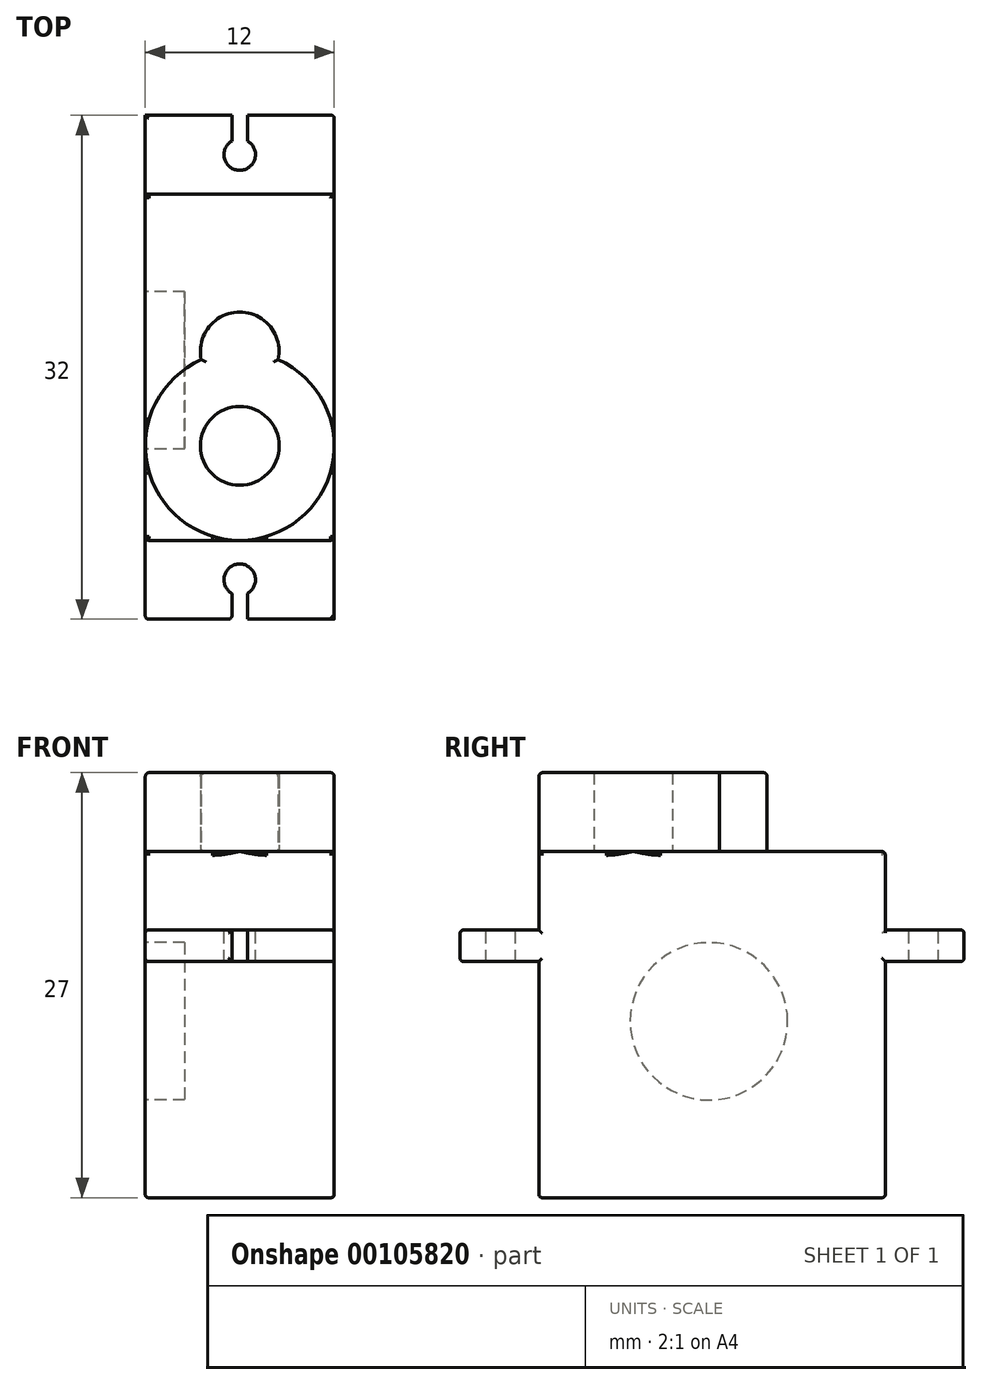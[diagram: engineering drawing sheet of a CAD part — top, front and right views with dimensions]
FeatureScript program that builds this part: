
annotation { "Feature Type Name" : "Feature", "Feature Type Description" : "" }
export const myFeature = defineFeature(function(context is Context, id is Id, definition is map)
    precondition{}
    {
        {
            var Q0;
            Q0=qCreatedBy(makeId("Top.planeOp"),FACE);
            var sketch = newSketch(context, id + "F0", { "sketchPlane" : qUnion([Q0])});
            skLineSegment(sketch, "E0.bottom", {"start": v(-8.25, -0.4) * mm, "end": v(3.75, -0.4) * mm});
            skLineSegment(sketch, "E0.top", {"start": v(-8.25, -22.4) * mm, "end": v(3.75, -22.4) * mm});
            skLineSegment(sketch, "E0.left", {"start": v(-8.25, -0.4) * mm, "end": v(-8.25, -22.4) * mm});
            skLineSegment(sketch, "E0.right", {"start": v(3.75, -0.4) * mm, "end": v(3.75, -22.4) * mm});
            skSolve(sketch);
        }
        {
            var Q0;
            Q0=makeQuery(id+"F0.imprint","IMPRINT",FACE,{"disambiguationData":[TD([[makeQuery(id+"F0.imprint","IMPRINT",EDGE,{"derivedFrom":sQuery(id+"F0.wireOp",EDGE,"E0.bottom")}),-1.0]])]});
            extrude(context, id + "F1", {"entities" : qUnion([Q0]), "depth" : 22 * mm});
        }
        {
            var Q0;
            Q0=makeQuery(id+"F1.opExtrude","CAP_FACE",FACE,{"disambiguationData":[OSD([sQuery(id+"F0.wireOp",EDGE,"E0.bottom"),sQuery(id+"F0.wireOp",EDGE,"E0.top"),sQuery(id+"F0.wireOp",EDGE,"E0.left"),sQuery(id+"F0.wireOp",EDGE,"E0.right")])],"isStart":false});
            var sketch = newSketch(context, id + "F2", { "sketchPlane" : qUnion([Q0])});
            skCircle(sketch, "E1", {"center": v(-2.25, -16.4) * mm, "radius": 6 * mm});
            skCircle(sketch, "E2", {"center": v(-2.25, -16.4) * mm, "radius": 2.5 * mm});
            skCircle(sketch, "E3", {"center": v(-2.25, -10.4) * mm, "radius": 2.5 * mm});
            skSolve(sketch);
        }
        {
            var Q0;
            {var subQ0=sQuery(id+"F2.wireOp",EDGE,"E3");var subQ1=sQuery(id+"F2.wireOp",EDGE,"E1");var subQ3=makeQuery(id+"F2.imprint","INTERSECT",VERTEX,{"disambiguationData":[OD(0.0)],"derivedFrom":[subQ1,subQ0]});Q0=makeQuery(id+"F2.imprint","IMPRINT",FACE,{"disambiguationData":[TD([[makeQuery(id+"F2.imprint","IMPRINT",EDGE,{"disambiguationData":[TD([[subQ3,-1.0]])],"derivedFrom":subQ1}),-1.0]])]});}
            var Q1;
            {var subQ0=sQuery(id+"F2.wireOp",EDGE,"E3");var subQ1=sQuery(id+"F2.wireOp",EDGE,"E1");var subQ3=makeQuery(id+"F2.imprint","INTERSECT",VERTEX,{"disambiguationData":[OD(0.0)],"derivedFrom":[subQ1,subQ0]});Q1=makeQuery(id+"F2.imprint","IMPRINT",FACE,{"disambiguationData":[TD([[makeQuery(id+"F2.imprint","IMPRINT",EDGE,{"disambiguationData":[TD([[subQ3,-1.0]])],"derivedFrom":subQ1}),1.0]])]});}
            var Q2;
            Q2=makeQuery(id+"F2.imprint","IMPRINT",FACE,{"disambiguationData":[TD([[makeQuery(id+"F2.imprint","IMPRINT",EDGE,{"derivedFrom":sQuery(id+"F2.wireOp",EDGE,"E2")}),-1.0]])]});
            extrude(context, id + "F3", {"entities" : qUnion([Q0, Q1, Q2]), "operationType" : NewBodyOperationType.ADD, "depth" : 5 * mm});
        }
        {
            var Q0;
            Q0=makeQuery(id+"F3.opExtrude","CAP_EDGE",EDGE,{"disambiguationData":[OSD([sQuery(id+"F2.wireOp",EDGE,"E1")])],"isStart":false});
            var Q1;
            Q1=makeQuery(id+"F3.opExtrude","CAP_EDGE",EDGE,{"disambiguationData":[OSD([sQuery(id+"F2.wireOp",EDGE,"E3")])],"isStart":false});
            var Q2;
            {var subQ0=sQuery(id+"F0.wireOp",EDGE,"E0.right");var subQ1=sQuery(id+"F0.wireOp",EDGE,"E0.bottom");Q2=makeQuery(id+"F3.boolean.opBoolean","SPLIT",EDGE,{"disambiguationData":[TD([makeQuery(id+"F1.opExtrude","SWEPT_FACE",FACE,{"disambiguationData":[OSD([subQ1])]})])],"derivedFrom":makeQuery(id+"F1.opExtrude","CAP_EDGE",EDGE,{"disambiguationData":[OSD([subQ0])],"isStart":false})});}
            var Q3;
            Q3=makeQuery(id+"F1.opExtrude","CAP_EDGE",EDGE,{"disambiguationData":[OSD([sQuery(id+"F0.wireOp",EDGE,"E0.bottom")])],"isStart":false});
            var Q4;
            {var subQ0=sQuery(id+"F0.wireOp",EDGE,"E0.left");var subQ1=sQuery(id+"F0.wireOp",EDGE,"E0.bottom");Q4=makeQuery(id+"F3.boolean.opBoolean","SPLIT",EDGE,{"disambiguationData":[TD([makeQuery(id+"F1.opExtrude","SWEPT_FACE",FACE,{"disambiguationData":[OSD([subQ1])]})])],"derivedFrom":makeQuery(id+"F1.opExtrude","CAP_EDGE",EDGE,{"disambiguationData":[OSD([subQ0])],"isStart":false})});}
            var Q5;
            {var subQ0=sQuery(id+"F0.wireOp",EDGE,"E0.right");var subQ1=sQuery(id+"F0.wireOp",EDGE,"E0.top");Q5=makeQuery(id+"F3.boolean.opBoolean","SPLIT",EDGE,{"disambiguationData":[TD([makeQuery(id+"F1.opExtrude","SWEPT_FACE",FACE,{"disambiguationData":[OSD([subQ1])]})])],"derivedFrom":makeQuery(id+"F1.opExtrude","CAP_EDGE",EDGE,{"disambiguationData":[OSD([subQ0])],"isStart":false})});}
            var Q6;
            {var subQ0=sQuery(id+"F0.wireOp",EDGE,"E0.top");var subQ1=sQuery(id+"F0.wireOp",EDGE,"E0.right");Q6=makeQuery(id+"F3.boolean.opBoolean","SPLIT",EDGE,{"disambiguationData":[TD([makeQuery(id+"F1.opExtrude","SWEPT_FACE",FACE,{"disambiguationData":[OSD([subQ1])]})])],"derivedFrom":makeQuery(id+"F1.opExtrude","CAP_EDGE",EDGE,{"disambiguationData":[OSD([subQ0])],"isStart":false})});}
            var Q7;
            {var subQ0=sQuery(id+"F0.wireOp",EDGE,"E0.top");var subQ1=sQuery(id+"F0.wireOp",EDGE,"E0.left");Q7=makeQuery(id+"F3.boolean.opBoolean","SPLIT",EDGE,{"disambiguationData":[TD([makeQuery(id+"F1.opExtrude","SWEPT_FACE",FACE,{"disambiguationData":[OSD([subQ1])]})])],"derivedFrom":makeQuery(id+"F1.opExtrude","CAP_EDGE",EDGE,{"disambiguationData":[OSD([subQ0])],"isStart":false})});}
            var Q8;
            {var subQ0=sQuery(id+"F0.wireOp",EDGE,"E0.left");var subQ1=sQuery(id+"F0.wireOp",EDGE,"E0.top");Q8=makeQuery(id+"F3.boolean.opBoolean","SPLIT",EDGE,{"disambiguationData":[TD([makeQuery(id+"F1.opExtrude","SWEPT_FACE",FACE,{"disambiguationData":[OSD([subQ1])]})])],"derivedFrom":makeQuery(id+"F1.opExtrude","CAP_EDGE",EDGE,{"disambiguationData":[OSD([subQ0])],"isStart":false})});}
            fillet(context, id + "F4", {"entities" : qUnion([Q0, Q1, Q2, Q3, Q4, Q5, Q6, Q7, Q8]), "radius" : .25 * mm, "tangentPropagation" : true, "allowEdgeOverflow" : false});
        }
        {
            var Q0;
            Q0=makeQuery(id+"F1.opExtrude","SWEPT_FACE",FACE,{"disambiguationData":[OSD([sQuery(id+"F0.wireOp",EDGE,"E0.bottom")])]});
            var sketch = newSketch(context, id + "F5", { "sketchPlane" : qUnion([Q0])});
            skLineSegment(sketch, "E4.bottom", {"start": v(-3.75, 17) * mm, "end": v(8.25, 17) * mm});
            skLineSegment(sketch, "E4.top", {"start": v(-3.75, 15) * mm, "end": v(8.25, 15) * mm});
            skLineSegment(sketch, "E4.left", {"start": v(-3.75, 17) * mm, "end": v(-3.75, 15) * mm});
            skLineSegment(sketch, "E4.right", {"start": v(8.25, 17) * mm, "end": v(8.25, 15) * mm});
            skSolve(sketch);
        }
        {
            var Q0;
            Q0=makeQuery(id+"F1.opExtrude","SWEPT_FACE",FACE,{"disambiguationData":[OSD([sQuery(id+"F0.wireOp",EDGE,"E0.top")])]});
            var sketch = newSketch(context, id + "F6", { "sketchPlane" : qUnion([Q0])});
            skLineSegment(sketch, "E5.bottom", {"start": v(-8.25, 17) * mm, "end": v(3.75, 17) * mm});
            skLineSegment(sketch, "E5.top", {"start": v(-8.25, 15) * mm, "end": v(3.75, 15) * mm});
            skLineSegment(sketch, "E5.left", {"start": v(-8.25, 17) * mm, "end": v(-8.25, 15) * mm});
            skLineSegment(sketch, "E5.right", {"start": v(3.75, 17) * mm, "end": v(3.75, 15) * mm});
            skSolve(sketch);
        }
        {
            var Q0;
            Q0=makeQuery(id+"F6.imprint","IMPRINT",FACE,{"disambiguationData":[TD([[makeQuery(id+"F6.imprint","IMPRINT",EDGE,{"derivedFrom":sQuery(id+"F6.wireOp",EDGE,"E5.bottom")}),-1.0]])]});
            extrude(context, id + "F7", {"entities" : qUnion([Q0]), "operationType" : NewBodyOperationType.ADD, "depth" : 5 * mm});
        }
        {
            var Q0;
            Q0=makeQuery(id+"F5.imprint","IMPRINT",FACE,{"disambiguationData":[TD([[makeQuery(id+"F5.imprint","IMPRINT",EDGE,{"derivedFrom":sQuery(id+"F5.wireOp",EDGE,"E4.bottom")}),-1.0]])]});
            extrude(context, id + "F8", {"entities" : qUnion([Q0]), "operationType" : NewBodyOperationType.ADD, "depth" : 5 * mm});
        }
        {
            var Q0;
            Q0=makeQuery(id+"F7.opExtrude","SWEPT_FACE",FACE,{"disambiguationData":[OSD([sQuery(id+"F6.wireOp",EDGE,"E5.bottom")])]});
            var sketch = newSketch(context, id + "F9", { "sketchPlane" : qUnion([Q0])});
            skCircle(sketch, "E6", {"center": v(-2.25, -24.9) * mm, "radius": 1 * mm});
            skLineSegment(sketch, "E7.bottom", {"start": v(-2.75, -25.77) * mm, "end": v(-1.75, -25.77) * mm});
            skLineSegment(sketch, "E7.top", {"start": v(-2.75, -27.4) * mm, "end": v(-1.75, -27.4) * mm});
            skLineSegment(sketch, "E7.left", {"start": v(-2.75, -25.77) * mm, "end": v(-2.75, -27.4) * mm});
            skLineSegment(sketch, "E7.right", {"start": v(-1.75, -25.77) * mm, "end": v(-1.75, -27.4) * mm});
            skSolve(sketch);
        }
        {
            var Q0;
            {var subQ0=sQuery(id+"F9.wireOp",EDGE,"E7.bottom");Q0=makeQuery(id+"F9.imprint","IMPRINT",FACE,{"disambiguationData":[TD([[makeQuery(id+"F9.imprint","IMPRINT",EDGE,{"derivedFrom":subQ0}),1.0]])]});}
            var Q1;
            Q1=makeQuery(id+"F9.imprint","IMPRINT",FACE,{"disambiguationData":[TD([[makeQuery(id+"F9.imprint","IMPRINT",EDGE,{"derivedFrom":sQuery(id+"F9.wireOp",EDGE,"E7.top")}),1.0]])]});
            var Q2;
            {var subQ0=sQuery(id+"F9.wireOp",EDGE,"E7.bottom");Q2=makeQuery(id+"F9.imprint","IMPRINT",FACE,{"disambiguationData":[TD([[makeQuery(id+"F9.imprint","IMPRINT",EDGE,{"derivedFrom":subQ0}),-1.0]])]});}
            extrude(context, id + "F10", {"entities" : qUnion([Q0, Q1, Q2]), "operationType" : NewBodyOperationType.REMOVE, "oppositeDirection" : true, "depth" : 2 * mm});
        }
        {
            var Q0;
            Q0=makeQuery(id+"F8.opExtrude","SWEPT_FACE",FACE,{"disambiguationData":[OSD([sQuery(id+"F5.wireOp",EDGE,"E4.bottom")])]});
            var sketch = newSketch(context, id + "F11", { "sketchPlane" : qUnion([Q0])});
            skCircle(sketch, "E8", {"center": v(-2.25, 2.1) * mm, "radius": 1 * mm});
            skLineSegment(sketch, "E9.bottom", {"start": v(-2.75, 4.6) * mm, "end": v(-1.75, 4.6) * mm});
            skLineSegment(sketch, "E9.top", {"start": v(-2.75, 2.6) * mm, "end": v(-1.75, 2.6) * mm});
            skLineSegment(sketch, "E9.left", {"start": v(-2.75, 4.6) * mm, "end": v(-2.75, 2.6) * mm});
            skLineSegment(sketch, "E9.right", {"start": v(-1.75, 4.6) * mm, "end": v(-1.75, 2.6) * mm});
            skSolve(sketch);
        }
        {
            var Q0;
            Q0=qSketchRegion(id+"F11",true);
            extrude(context, id + "F12", {"entities" : qUnion([Q0]), "operationType" : NewBodyOperationType.REMOVE, "oppositeDirection" : true, "depth" : 2 * mm});
        }
        {
            var Q0;
            Q0=makeQuery(id+"F8.opExtrude","SWEPT_EDGE",EDGE,{"disambiguationData":[OSD([sQuery(id+"F0.wireOp",EDGE,"E0.bottom"),sQuery(id+"F0.wireOp",EDGE,"E0.left"),sQuery(id+"F5.wireOp",EDGE,"E4.bottom"),sQuery(id+"F5.wireOp",EDGE,"E4.right")])]});
            var Q1;
            {var subQ0=sQuery(id+"F5.wireOp",EDGE,"E4.bottom");Q1=makeQuery(id+"F12.boolean.opBoolean","SPLIT",EDGE,{"disambiguationData":[TD([makeQuery(id+"F1.opExtrude","SWEPT_FACE",FACE,{"disambiguationData":[OSD([sQuery(id+"F0.wireOp",EDGE,"E0.left")])]})])],"derivedFrom":makeQuery(id+"F8.opExtrude","CAP_EDGE",EDGE,{"disambiguationData":[OSD([subQ0])],"isStart":false})});}
            var Q2;
            Q2=makeQuery(id+"F12.boolean.opBoolean","COPY",EDGE,{"derivedFrom":makeQuery(id+"F12.opExtrude","CAP_EDGE",EDGE,{"disambiguationData":[OSD([sQuery(id+"F11.wireOp",EDGE,"E9.left")])],"isStart":true})});
            var Q3;
            Q3=makeQuery(id+"F12.boolean.opBoolean","COPY",EDGE,{"derivedFrom":makeQuery(id+"F12.opExtrude","CAP_EDGE",EDGE,{"disambiguationData":[OSD([sQuery(id+"F11.wireOp",EDGE,"E8")])],"isStart":true})});
            var Q4;
            Q4=makeQuery(id+"F12.boolean.opBoolean","COPY",EDGE,{"derivedFrom":makeQuery(id+"F12.opExtrude","CAP_EDGE",EDGE,{"disambiguationData":[OSD([sQuery(id+"F11.wireOp",EDGE,"E9.right")])],"isStart":true})});
            var Q5;
            {var subQ0=sQuery(id+"F5.wireOp",EDGE,"E4.bottom");Q5=makeQuery(id+"F12.boolean.opBoolean","SPLIT",EDGE,{"disambiguationData":[TD([makeQuery(id+"F1.opExtrude","SWEPT_FACE",FACE,{"disambiguationData":[OSD([sQuery(id+"F0.wireOp",EDGE,"E0.right")])]})])],"derivedFrom":makeQuery(id+"F8.opExtrude","CAP_EDGE",EDGE,{"disambiguationData":[OSD([subQ0])],"isStart":false})});}
            var Q6;
            Q6=makeQuery(id+"F8.opExtrude","SWEPT_EDGE",EDGE,{"disambiguationData":[OSD([sQuery(id+"F0.wireOp",EDGE,"E0.bottom"),sQuery(id+"F0.wireOp",EDGE,"E0.right"),sQuery(id+"F5.wireOp",EDGE,"E4.bottom"),sQuery(id+"F5.wireOp",EDGE,"E4.left")])]});
            var Q7;
            Q7=makeQuery(id+"F7.opExtrude","SWEPT_EDGE",EDGE,{"disambiguationData":[OSD([sQuery(id+"F0.wireOp",EDGE,"E0.top"),sQuery(id+"F0.wireOp",EDGE,"E0.right"),sQuery(id+"F6.wireOp",EDGE,"E5.bottom"),sQuery(id+"F6.wireOp",EDGE,"E5.right")])]});
            var Q8;
            {var subQ0=sQuery(id+"F6.wireOp",EDGE,"E5.bottom");Q8=makeQuery(id+"F10.boolean.opBoolean","SPLIT",EDGE,{"disambiguationData":[TD([makeQuery(id+"F1.opExtrude","SWEPT_FACE",FACE,{"disambiguationData":[OSD([sQuery(id+"F0.wireOp",EDGE,"E0.right")])]})])],"derivedFrom":makeQuery(id+"F7.opExtrude","CAP_EDGE",EDGE,{"disambiguationData":[OSD([subQ0])],"isStart":false})});}
            var Q9;
            {var subQ0=sQuery(id+"F6.wireOp",EDGE,"E5.top");Q9=makeQuery(id+"F10.boolean.opBoolean","SPLIT",EDGE,{"disambiguationData":[TD([makeQuery(id+"F1.opExtrude","SWEPT_FACE",FACE,{"disambiguationData":[OSD([sQuery(id+"F0.wireOp",EDGE,"E0.right")])]})])],"derivedFrom":makeQuery(id+"F7.opExtrude","CAP_EDGE",EDGE,{"disambiguationData":[OSD([subQ0])],"isStart":false})});}
            var Q10;
            Q10=makeQuery(id+"F7.opExtrude","SWEPT_EDGE",EDGE,{"disambiguationData":[OSD([sQuery(id+"F0.wireOp",EDGE,"E0.top"),sQuery(id+"F0.wireOp",EDGE,"E0.right"),sQuery(id+"F6.wireOp",EDGE,"E5.top"),sQuery(id+"F6.wireOp",EDGE,"E5.right")])]});
            var Q11;
            Q11=makeQuery(id+"F10.boolean.opBoolean","COPY",EDGE,{"derivedFrom":makeQuery(id+"F10.opExtrude","SWEPT_EDGE",EDGE,{"disambiguationData":[OSD([sQuery(id+"F6.wireOp",EDGE,"E5.bottom"),sQuery(id+"F9.wireOp",EDGE,"E7.top"),sQuery(id+"F9.wireOp",EDGE,"E7.right")])]})});
            var Q12;
            Q12=makeQuery(id+"F10.boolean.opBoolean","COPY",EDGE,{"derivedFrom":makeQuery(id+"F10.opExtrude","SWEPT_EDGE",EDGE,{"disambiguationData":[OSD([sQuery(id+"F6.wireOp",EDGE,"E5.bottom"),sQuery(id+"F9.wireOp",EDGE,"E7.top"),sQuery(id+"F9.wireOp",EDGE,"E7.left")])]})});
            var Q13;
            Q13=makeQuery(id+"F10.boolean.opBoolean","COPY",EDGE,{"derivedFrom":makeQuery(id+"F10.opExtrude","CAP_EDGE",EDGE,{"disambiguationData":[OSD([sQuery(id+"F9.wireOp",EDGE,"E7.left")])],"isStart":true})});
            var Q14;
            Q14=makeQuery(id+"F10.boolean.opBoolean","COPY",EDGE,{"derivedFrom":makeQuery(id+"F10.opExtrude","CAP_EDGE",EDGE,{"disambiguationData":[OSD([sQuery(id+"F9.wireOp",EDGE,"E6")])],"isStart":true})});
            var Q15;
            Q15=makeQuery(id+"F10.boolean.opBoolean","COPY",EDGE,{"derivedFrom":makeQuery(id+"F10.opExtrude","CAP_EDGE",EDGE,{"disambiguationData":[OSD([sQuery(id+"F9.wireOp",EDGE,"E7.left")])],"isStart":false})});
            var Q16;
            Q16=makeQuery(id+"F10.boolean.opBoolean","COPY",EDGE,{"derivedFrom":makeQuery(id+"F10.opExtrude","CAP_EDGE",EDGE,{"disambiguationData":[OSD([sQuery(id+"F9.wireOp",EDGE,"E6")])],"isStart":false})});
            var Q17;
            {var subQ0=sQuery(id+"F6.wireOp",EDGE,"E5.top");Q17=makeQuery(id+"F10.boolean.opBoolean","SPLIT",EDGE,{"disambiguationData":[TD([makeQuery(id+"F1.opExtrude","SWEPT_FACE",FACE,{"disambiguationData":[OSD([sQuery(id+"F0.wireOp",EDGE,"E0.left")])]})])],"derivedFrom":makeQuery(id+"F7.opExtrude","CAP_EDGE",EDGE,{"disambiguationData":[OSD([subQ0])],"isStart":false})});}
            var Q18;
            {var subQ0=sQuery(id+"F6.wireOp",EDGE,"E5.bottom");Q18=makeQuery(id+"F10.boolean.opBoolean","SPLIT",EDGE,{"disambiguationData":[TD([makeQuery(id+"F1.opExtrude","SWEPT_FACE",FACE,{"disambiguationData":[OSD([sQuery(id+"F0.wireOp",EDGE,"E0.left")])]})])],"derivedFrom":makeQuery(id+"F7.opExtrude","CAP_EDGE",EDGE,{"disambiguationData":[OSD([subQ0])],"isStart":false})});}
            var Q19;
            Q19=makeQuery(id+"F7.opExtrude","CAP_EDGE",EDGE,{"disambiguationData":[OSD([sQuery(id+"F6.wireOp",EDGE,"E5.left")])],"isStart":false});
            var Q20;
            {var subQ0=sQuery(id+"F0.wireOp",EDGE,"E0.top");var subQ1=sQuery(id+"F0.wireOp",EDGE,"E0.right");Q20=makeQuery(id+"F7.boolean.opBoolean","SPLIT",EDGE,{"disambiguationData":[TD([makeQuery(id+"F7.opExtrude","SWEPT_FACE",FACE,{"disambiguationData":[OSD([sQuery(id+"F6.wireOp",EDGE,"E5.top")])]})])],"derivedFrom":makeQuery(id+"F1.opExtrude","SWEPT_EDGE",EDGE,{"disambiguationData":[OSD([subQ0,subQ1])]})});}
            var Q21;
            {var subQ0=sQuery(id+"F0.wireOp",EDGE,"E0.top");var subQ1=sQuery(id+"F0.wireOp",EDGE,"E0.right");Q21=makeQuery(id+"F7.boolean.opBoolean","SPLIT",EDGE,{"disambiguationData":[TD([makeQuery(id+"F7.opExtrude","SWEPT_FACE",FACE,{"disambiguationData":[OSD([sQuery(id+"F6.wireOp",EDGE,"E5.bottom")])]})])],"derivedFrom":makeQuery(id+"F1.opExtrude","SWEPT_EDGE",EDGE,{"disambiguationData":[OSD([subQ0,subQ1])]})});}
            var Q22;
            {var subQ0=sQuery(id+"F0.wireOp",EDGE,"E0.top");var subQ1=sQuery(id+"F0.wireOp",EDGE,"E0.left");Q22=makeQuery(id+"F7.boolean.opBoolean","SPLIT",EDGE,{"disambiguationData":[TD([makeQuery(id+"F7.opExtrude","SWEPT_FACE",FACE,{"disambiguationData":[OSD([sQuery(id+"F6.wireOp",EDGE,"E5.bottom")])]})])],"derivedFrom":makeQuery(id+"F1.opExtrude","SWEPT_EDGE",EDGE,{"disambiguationData":[OSD([subQ0,subQ1])]})});}
            var Q23;
            Q23=makeQuery(id+"F10.boolean.opBoolean","COPY",EDGE,{"derivedFrom":makeQuery(id+"F10.opExtrude","CAP_EDGE",EDGE,{"disambiguationData":[OSD([sQuery(id+"F9.wireOp",EDGE,"E7.right")])],"isStart":false})});
            var Q24;
            Q24=makeQuery(id+"F7.opExtrude","SWEPT_EDGE",EDGE,{"disambiguationData":[OSD([sQuery(id+"F0.wireOp",EDGE,"E0.top"),sQuery(id+"F0.wireOp",EDGE,"E0.left"),sQuery(id+"F6.wireOp",EDGE,"E5.top"),sQuery(id+"F6.wireOp",EDGE,"E5.left")])]});
            var Q25;
            Q25=makeQuery(id+"F7.opExtrude","SWEPT_EDGE",EDGE,{"disambiguationData":[OSD([sQuery(id+"F0.wireOp",EDGE,"E0.top"),sQuery(id+"F0.wireOp",EDGE,"E0.left"),sQuery(id+"F6.wireOp",EDGE,"E5.bottom"),sQuery(id+"F6.wireOp",EDGE,"E5.left")])]});
            var Q26;
            {var subQ0=sQuery(id+"F0.wireOp",EDGE,"E0.top");var subQ1=sQuery(id+"F0.wireOp",EDGE,"E0.left");Q26=makeQuery(id+"F7.boolean.opBoolean","SPLIT",EDGE,{"disambiguationData":[TD([makeQuery(id+"F7.opExtrude","SWEPT_FACE",FACE,{"disambiguationData":[OSD([sQuery(id+"F6.wireOp",EDGE,"E5.top")])]})])],"derivedFrom":makeQuery(id+"F1.opExtrude","SWEPT_EDGE",EDGE,{"disambiguationData":[OSD([subQ0,subQ1])]})});}
            var Q27;
            Q27=makeQuery(id+"F1.opExtrude","CAP_EDGE",EDGE,{"disambiguationData":[OSD([sQuery(id+"F0.wireOp",EDGE,"E0.left")])],"isStart":true});
            var Q28;
            Q28=makeQuery(id+"F1.opExtrude","CAP_EDGE",EDGE,{"disambiguationData":[OSD([sQuery(id+"F0.wireOp",EDGE,"E0.top")])],"isStart":true});
            var Q29;
            {var subQ0=sQuery(id+"F0.wireOp",EDGE,"E0.bottom");var subQ1=sQuery(id+"F0.wireOp",EDGE,"E0.left");Q29=makeQuery(id+"F8.boolean.opBoolean","SPLIT",EDGE,{"disambiguationData":[TD([makeQuery(id+"F8.opExtrude","SWEPT_FACE",FACE,{"disambiguationData":[OSD([sQuery(id+"F5.wireOp",EDGE,"E4.top")])]})])],"derivedFrom":makeQuery(id+"F1.opExtrude","SWEPT_EDGE",EDGE,{"disambiguationData":[OSD([subQ0,subQ1])]})});}
            var Q30;
            Q30=makeQuery(id+"F8.opExtrude","SWEPT_EDGE",EDGE,{"disambiguationData":[OSD([sQuery(id+"F0.wireOp",EDGE,"E0.bottom"),sQuery(id+"F0.wireOp",EDGE,"E0.left"),sQuery(id+"F5.wireOp",EDGE,"E4.top"),sQuery(id+"F5.wireOp",EDGE,"E4.right")])]});
            var Q31;
            {var subQ0=sQuery(id+"F5.wireOp",EDGE,"E4.top");Q31=makeQuery(id+"F12.boolean.opBoolean","SPLIT",EDGE,{"disambiguationData":[TD([makeQuery(id+"F1.opExtrude","SWEPT_FACE",FACE,{"disambiguationData":[OSD([sQuery(id+"F0.wireOp",EDGE,"E0.left")])]})])],"derivedFrom":makeQuery(id+"F8.opExtrude","CAP_EDGE",EDGE,{"disambiguationData":[OSD([subQ0])],"isStart":false})});}
            var Q32;
            Q32=makeQuery(id+"F12.boolean.opBoolean","COPY",EDGE,{"derivedFrom":makeQuery(id+"F12.opExtrude","CAP_EDGE",EDGE,{"disambiguationData":[OSD([sQuery(id+"F11.wireOp",EDGE,"E8")])],"isStart":false})});
            var Q33;
            Q33=makeQuery(id+"F12.boolean.opBoolean","COPY",EDGE,{"derivedFrom":makeQuery(id+"F12.opExtrude","CAP_EDGE",EDGE,{"disambiguationData":[OSD([sQuery(id+"F11.wireOp",EDGE,"E9.left")])],"isStart":false})});
            var Q34;
            Q34=makeQuery(id+"F12.boolean.opBoolean","COPY",EDGE,{"derivedFrom":makeQuery(id+"F12.opExtrude","CAP_EDGE",EDGE,{"disambiguationData":[OSD([sQuery(id+"F11.wireOp",EDGE,"E9.right")])],"isStart":false})});
            var Q35;
            {var subQ0=sQuery(id+"F0.wireOp",EDGE,"E0.bottom");var subQ1=sQuery(id+"F0.wireOp",EDGE,"E0.left");Q35=makeQuery(id+"F8.boolean.opBoolean","SPLIT",EDGE,{"disambiguationData":[TD([makeQuery(id+"F4.opFillet","BLEND_FACE",FACE,{"disambiguationData":[OSD([subQ0])]})])],"derivedFrom":makeQuery(id+"F1.opExtrude","SWEPT_EDGE",EDGE,{"disambiguationData":[OSD([subQ0,subQ1])]})});}
            var Q36;
            {var subQ0=sQuery(id+"F0.wireOp",EDGE,"E0.bottom");var subQ1=sQuery(id+"F0.wireOp",EDGE,"E0.right");Q36=makeQuery(id+"F8.boolean.opBoolean","SPLIT",EDGE,{"disambiguationData":[TD([makeQuery(id+"F8.opExtrude","SWEPT_FACE",FACE,{"disambiguationData":[OSD([sQuery(id+"F5.wireOp",EDGE,"E4.top")])]})])],"derivedFrom":makeQuery(id+"F1.opExtrude","SWEPT_EDGE",EDGE,{"disambiguationData":[OSD([subQ0,subQ1])]})});}
            var Q37;
            Q37=makeQuery(id+"F1.opExtrude","CAP_EDGE",EDGE,{"disambiguationData":[OSD([sQuery(id+"F0.wireOp",EDGE,"E0.right")])],"isStart":true});
            var Q38;
            Q38=makeQuery(id+"F1.opExtrude","CAP_EDGE",EDGE,{"disambiguationData":[OSD([sQuery(id+"F0.wireOp",EDGE,"E0.bottom")])],"isStart":true});
            var Q39;
            Q39=makeQuery(id+"F8.opExtrude","SWEPT_EDGE",EDGE,{"disambiguationData":[OSD([sQuery(id+"F0.wireOp",EDGE,"E0.bottom"),sQuery(id+"F0.wireOp",EDGE,"E0.right"),sQuery(id+"F5.wireOp",EDGE,"E4.top"),sQuery(id+"F5.wireOp",EDGE,"E4.left")])]});
            var Q40;
            Q40=makeQuery(id+"F8.opExtrude","CAP_EDGE",EDGE,{"disambiguationData":[OSD([sQuery(id+"F5.wireOp",EDGE,"E4.left")])],"isStart":false});
            var Q41;
            {var subQ0=sQuery(id+"F5.wireOp",EDGE,"E4.top");Q41=makeQuery(id+"F12.boolean.opBoolean","SPLIT",EDGE,{"disambiguationData":[TD([makeQuery(id+"F1.opExtrude","SWEPT_FACE",FACE,{"disambiguationData":[OSD([sQuery(id+"F0.wireOp",EDGE,"E0.right")])]})])],"derivedFrom":makeQuery(id+"F8.opExtrude","CAP_EDGE",EDGE,{"disambiguationData":[OSD([subQ0])],"isStart":false})});}
            fillet(context, id + "F13", {"entities" : qUnion([Q0, Q1, Q2, Q3, Q4, Q5, Q6, Q7, Q8, Q9, Q10, Q11, Q12, Q13, Q14, Q15, Q16, Q17, Q18, Q19, Q20, Q21, Q22, Q23, Q24, Q25, Q26, Q27, Q28, Q29, Q30, Q31, Q32, Q33, Q34, Q35, Q36, Q37, Q38, Q39, Q40, Q41]), "radius" : .2 * mm, "tangentPropagation" : true, "allowEdgeOverflow" : false});
        }
        {
            var Q0;
            Q0=makeQuery(id+"F8.boolean.opBoolean","MERGE",FACE,{"derivedFrom":[makeQuery(id+"F7.boolean.opBoolean","MERGE",FACE,{"derivedFrom":[makeQuery(id+"F1.opExtrude","SWEPT_FACE",FACE,{"disambiguationData":[OSD([sQuery(id+"F0.wireOp",EDGE,"E0.left")])]}),makeQuery(id+"F7.opExtrude","SWEPT_FACE",FACE,{"disambiguationData":[OSD([sQuery(id+"F6.wireOp",EDGE,"E5.left")])]})]}),makeQuery(id+"F8.opExtrude","SWEPT_FACE",FACE,{"disambiguationData":[OSD([sQuery(id+"F5.wireOp",EDGE,"E4.right")])]})]});
            var sketch = newSketch(context, id + "F14", { "sketchPlane" : qUnion([Q0])});
            skCircle(sketch, "E10", {"center": v(11.6, 11.2) * mm, "radius": 5 * mm});
            skSolve(sketch);
        }
        {
            var Q0;
            Q0=makeQuery(id+"F14.imprint","IMPRINT",FACE,{"disambiguationData":[TD([[makeQuery(id+"F14.imprint","IMPRINT",EDGE,{"derivedFrom":sQuery(id+"F14.wireOp",EDGE,"E10")}),1.0]])]});
            extrude(context, id + "F15", {"entities" : qUnion([Q0]), "operationType" : NewBodyOperationType.REMOVE, "oppositeDirection" : true, "depth" : 2.5 * mm});
        }
    });
